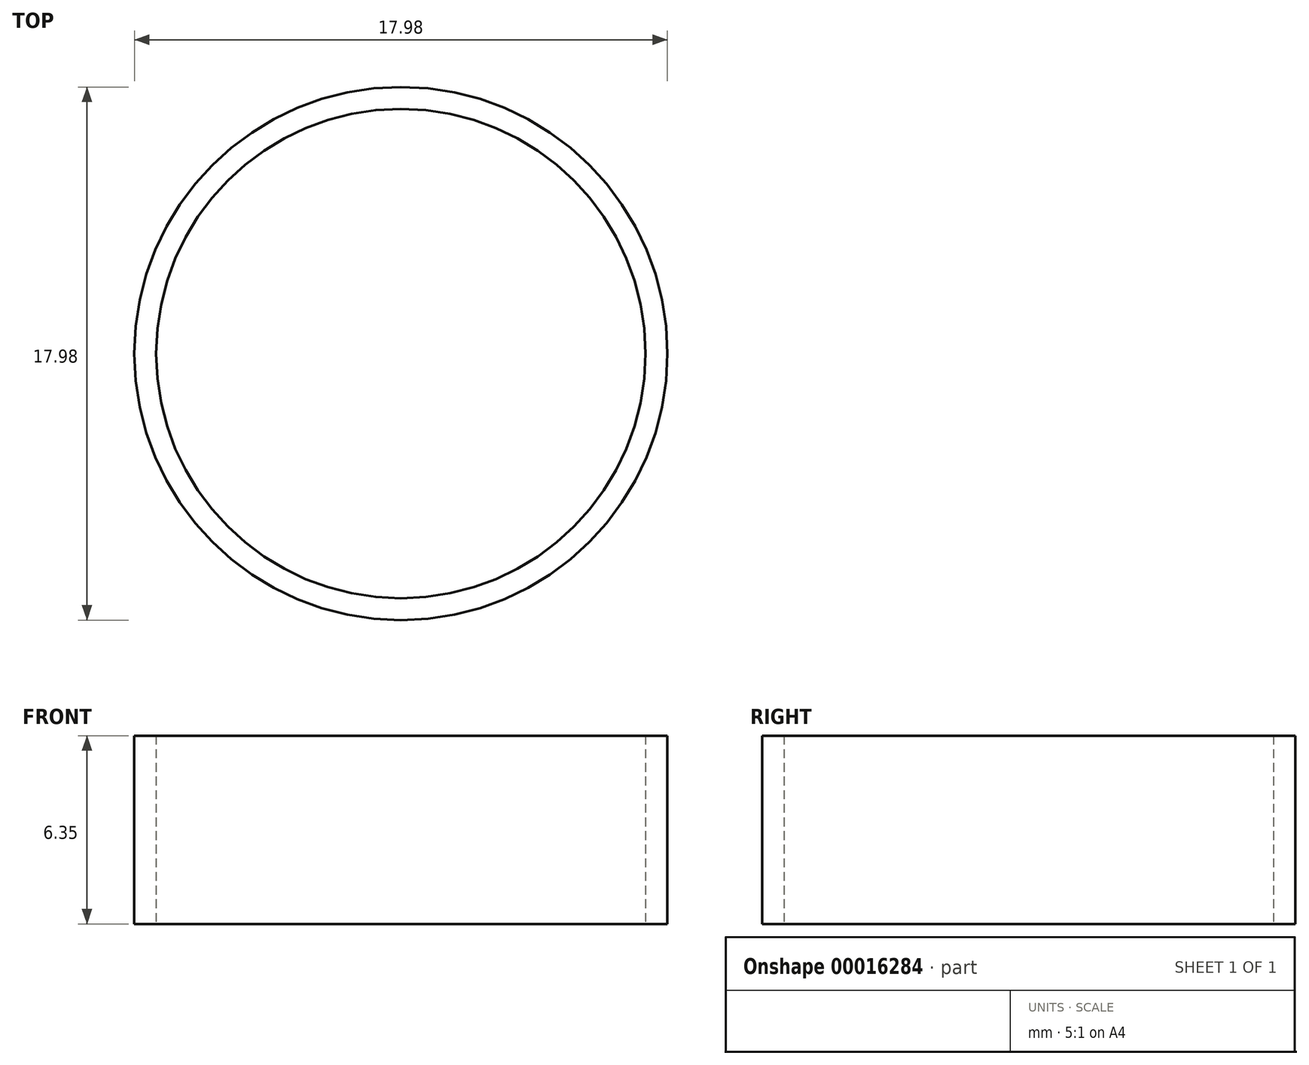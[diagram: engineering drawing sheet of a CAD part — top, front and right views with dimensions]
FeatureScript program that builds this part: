
annotation { "Feature Type Name" : "Feature", "Feature Type Description" : "" }
export const myFeature = defineFeature(function(context is Context, id is Id, definition is map)
    precondition{}
    {
        {
            var Q0;
            Q0=qCreatedBy(makeId("Front.planeOp"),FACE);
            var sketch = newSketch(context, id + "F0", { "sketchPlane" : qUnion([Q0])});
            skLineSegment(sketch, "E0", {"start": v(0, 0) * mm, "end": v(8.26, 0) * mm});
            skLineSegment(sketch, "E1", {"start": v(8.26, 0) * mm, "end": v(8.26, 6.35) * mm});
            skLineSegment(sketch, "E2", {"start": v(8.26, 6.35) * mm, "end": v(9, 6.35) * mm});
            skLineSegment(sketch, "E3", {"start": v(9, 6.35) * mm, "end": v(9, 0) * mm});
            skLineSegment(sketch, "E4", {"start": v(9, 0) * mm, "end": v(8.26, 0) * mm});
            skLineSegment(sketch, "E5", {"start": v(0, 0) * mm, "end": v(0, 6.35) * mm});
            skLineSegment(sketch, "E6", {"start": v(0, 6.35) * mm, "end": v(8.26, 6.35) * mm});
            skSolve(sketch);
        }
        {
            var Q0;
            Q0=makeQuery(id+"F0.imprint","IMPRINT",FACE,{"disambiguationData":[TD([[makeQuery(id+"F0.imprint","IMPRINT",EDGE,{"derivedFrom":sQuery(id+"F0.wireOp",EDGE,"E1")}),-1.0]])]});
            var Q1;
            Q1=sQuery(id+"F0.wireOp",EDGE,"E5");
            revolve(context, id + "F1", {"entities" : qUnion([Q0]), "axis" : qUnion([Q1]), "revolveType" : RevolveType.FULL});
        }
    });
